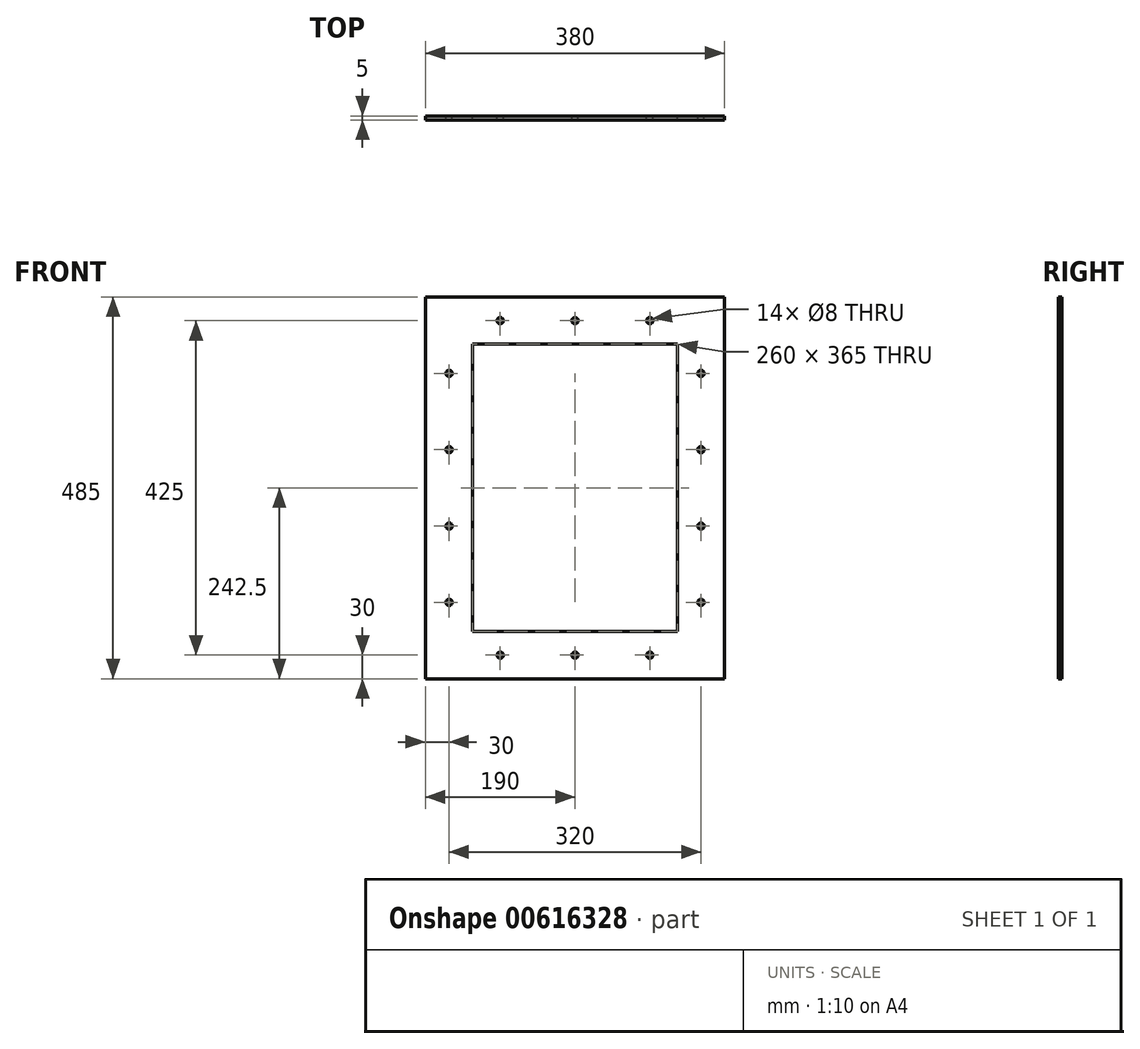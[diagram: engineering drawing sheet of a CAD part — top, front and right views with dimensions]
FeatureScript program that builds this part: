
annotation { "Feature Type Name" : "Feature", "Feature Type Description" : "" }
export const myFeature = defineFeature(function(context is Context, id is Id, definition is map)
    precondition{}
    {
        {
            var Q0;
            Q0=qCreatedBy(makeId("Front.planeOp"),FACE);
            var sketch = newSketch(context, id + "F0", { "sketchPlane" : qUnion([Q0])});
            skLineSegment(sketch, "E0.bottom", {"start": v(-130, 60) * mm, "end": v(130, 60) * mm});
            skLineSegment(sketch, "E0.top", {"start": v(-190, 0) * mm, "end": v(190, 0) * mm});
            skLineSegment(sketch, "E1", {"start": v(-190, 0) * mm, "end": v(-130, 60) * mm});
            skLineSegment(sketch, "E2", {"start": v(190, 0) * mm, "end": v(130, 60) * mm});
            skPoint(sketch, "E0.left.start.orphan", {"position": v(-194.91, 60) * mm});
            skCircle(sketch, "E3", {"center": v(-95, 30) * mm, "radius": 4 * mm});
            skPoint(sketch, "E3.centerSnap0", {"position": v(-160, 30) * mm});
            skCircle(sketch, "E4.1.0.0", {"center": v(0, 30) * mm, "radius": 4 * mm});
            skCircle(sketch, "E4.2.0.0", {"center": v(95, 30) * mm, "radius": 4 * mm});
            skLineSegment(sketch, "E4.direction1", {"start": v(-95, 30) * mm, "end": v(0, 30) * mm, "construction": true});
            skLineSegment(sketch, "E5", {"start": v(-190, 0) * mm, "end": v(-190, 485) * mm});
            skLineSegment(sketch, "E6", {"start": v(-190, 485) * mm, "end": v(190, 485) * mm});
            skLineSegment(sketch, "E7", {"start": v(190, 485) * mm, "end": v(190, 0) * mm});
            skLineSegment(sketch, "E8", {"start": v(130, 425) * mm, "end": v(-130, 425) * mm});
            skLineSegment(sketch, "E9", {"start": v(-130, 60) * mm, "end": v(-130, 425) * mm});
            skLineSegment(sketch, "E10", {"start": v(130, 425) * mm, "end": v(130, 60) * mm});
            skLineSegment(sketch, "E11", {"start": v(130, 425) * mm, "end": v(190, 485) * mm});
            skLineSegment(sketch, "E12", {"start": v(-130, 425) * mm, "end": v(-190, 485) * mm});
            skCircle(sketch, "E13", {"center": v(160, 388) * mm, "radius": 4 * mm});
            skPoint(sketch, "E13.centerSnap0", {"position": v(160, 455) * mm});
            skCircle(sketch, "E14.0.1.0", {"center": v(160, 291) * mm, "radius": 4 * mm});
            skCircle(sketch, "E14.0.2.0", {"center": v(160, 194) * mm, "radius": 4 * mm});
            skCircle(sketch, "E14.0.3.0", {"center": v(160, 97) * mm, "radius": 4 * mm});
            skLineSegment(sketch, "E14.direction1", {"start": v(160, 388) * mm, "end": v(185, 388) * mm, "construction": true});
            skLineSegment(sketch, "E14.direction2", {"start": v(160, 388) * mm, "end": v(160, 291) * mm, "construction": true});
            skCircle(sketch, "E15", {"center": v(-160, 388) * mm, "radius": 4 * mm});
            skPoint(sketch, "E15.centerSnap0", {"position": v(-160, 455) * mm});
            skCircle(sketch, "E16", {"center": v(-95, 455) * mm, "radius": 4 * mm});
            skCircle(sketch, "E17.0.1.0", {"center": v(-160, 291) * mm, "radius": 4 * mm});
            skCircle(sketch, "E17.0.2.0", {"center": v(-160, 194) * mm, "radius": 4 * mm});
            skCircle(sketch, "E17.0.3.0", {"center": v(-160, 97) * mm, "radius": 4 * mm});
            skLineSegment(sketch, "E17.direction1", {"start": v(-160, 388) * mm, "end": v(-135, 388) * mm, "construction": true});
            skLineSegment(sketch, "E17.direction2", {"start": v(-160, 388) * mm, "end": v(-160, 291) * mm, "construction": true});
            skCircle(sketch, "E18.1.0.0", {"center": v(0, 455) * mm, "radius": 4 * mm});
            skCircle(sketch, "E18.2.0.0", {"center": v(95, 455) * mm, "radius": 4 * mm});
            skLineSegment(sketch, "E18.direction1", {"start": v(-95, 455) * mm, "end": v(0, 455) * mm, "construction": true});
            skSolve(sketch);
        }
        {
            var Q0;
            Q0=makeQuery(id+"F0.imprint","IMPRINT",FACE,{"disambiguationData":[TD([[makeQuery(id+"F0.imprint","IMPRINT",EDGE,{"derivedFrom":sQuery(id+"F0.wireOp",EDGE,"E0.bottom")}),-1.0]])]});
            var Q1;
            Q1=makeQuery(id+"F0.imprint","IMPRINT",FACE,{"disambiguationData":[TD([[makeQuery(id+"F0.imprint","IMPRINT",EDGE,{"derivedFrom":sQuery(id+"F0.wireOp",EDGE,"E2")}),-1.0]])]});
            var Q2;
            Q2=makeQuery(id+"F0.imprint","IMPRINT",FACE,{"disambiguationData":[TD([[makeQuery(id+"F0.imprint","IMPRINT",EDGE,{"derivedFrom":sQuery(id+"F0.wireOp",EDGE,"E1")}),1.0]])]});
            var Q3;
            Q3=makeQuery(id+"F0.imprint","IMPRINT",FACE,{"disambiguationData":[TD([[makeQuery(id+"F0.imprint","IMPRINT",EDGE,{"derivedFrom":sQuery(id+"F0.wireOp",EDGE,"E6")}),-1.0]])]});
            extrude(context, id + "F1", {"entities" : qUnion([Q0, Q1, Q2, Q3]), "endBound" : BoundingType.SYMMETRIC, "depth" : 5 * mm, "offsetDistance" : 25 * mm});
        }
    });
